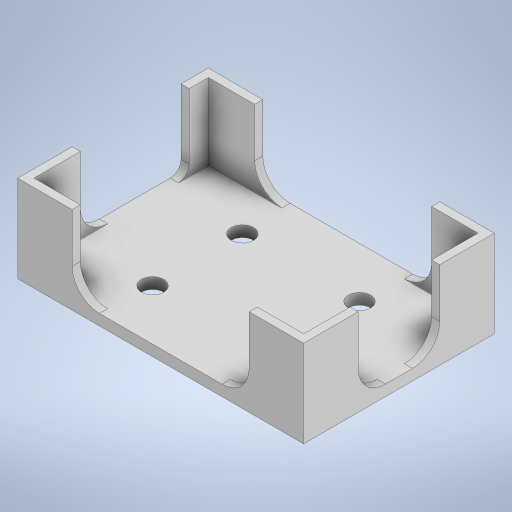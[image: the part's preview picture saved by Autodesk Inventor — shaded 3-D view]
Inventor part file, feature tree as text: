
AUTODESK INVENTOR PART (.ipt)
format: ipt  version: 2024.2 (Build 282272000, 272)  size: 361,984 bytes
history: native  units: mm
features: extrude x5, sketch x5, fillet x2
ambient origin geometry x8: Origin, YZ Plane, XZ Plane, XY Plane, X Axis, Y Axis, Z Axis, Center Point
bodies: Solid1 (feature_tree)
feature tree (12):
  extrude  "Extrusion1"  Depth=48.0mm
  extrude  "Extrusion3"  Depth=4.7mm
  extrude  "Extrusion4"  Depth=4.7mm
  fillet  "Fillet1"  Radius=33.0mm
  extrude  "remove legs"  Depth=7.5mm
  extrude  "Extrusion6"  Depth=4.0mm
  fillet  "Fillet2"  Radius=7.5mm
  sketch  "Sketch1"  dims[d0=58.0mm d1=48.0mm]
  sketch  "Sketch2"  dims[d2=4.7mm d3=4.7mm]
  sketch  "Sketch3"  dims[d4=4.7mm d5=4.7mm d6=33.0mm]
  sketch  "Sketch4"  dims[d7=43.0mm d8=7.5mm]
  sketch  "Sketch5"  dims[d9=7.5mm d10=7.5mm d11=7.5mm d12=7.500001mm d13=7.500001mm d14=10.0mm d15=10.0mm d16=10.0mm d17=10.0mm d18=12.0mm d19=0.0mm d20=105.0mm d21=70.0mm d22=18.5mm d23=31.0mm d26=4.0mm d27=0.0mm d28=20.0mm d37=3.0mm d45=28.0mm d46=0.0mm d47=10.0mm d48=20.0mm d49=3.0mm d50=3.0mm d51=3.0mm d52=3.0mm d53=20.0mm d54=20.0mm d55=20.0mm d56=20.0mm d57=3.0mm d58=3.0mm d59=100.0mm d60=15.0mm d61=25.0mm d62=0.0mm d63=8.2mm d64=8.2mm d65=8.2mm d66=8.2mm d67=4.0mm d68=0.0mm d69=10.0mm d70=7.0mm d71=4.0mm]
